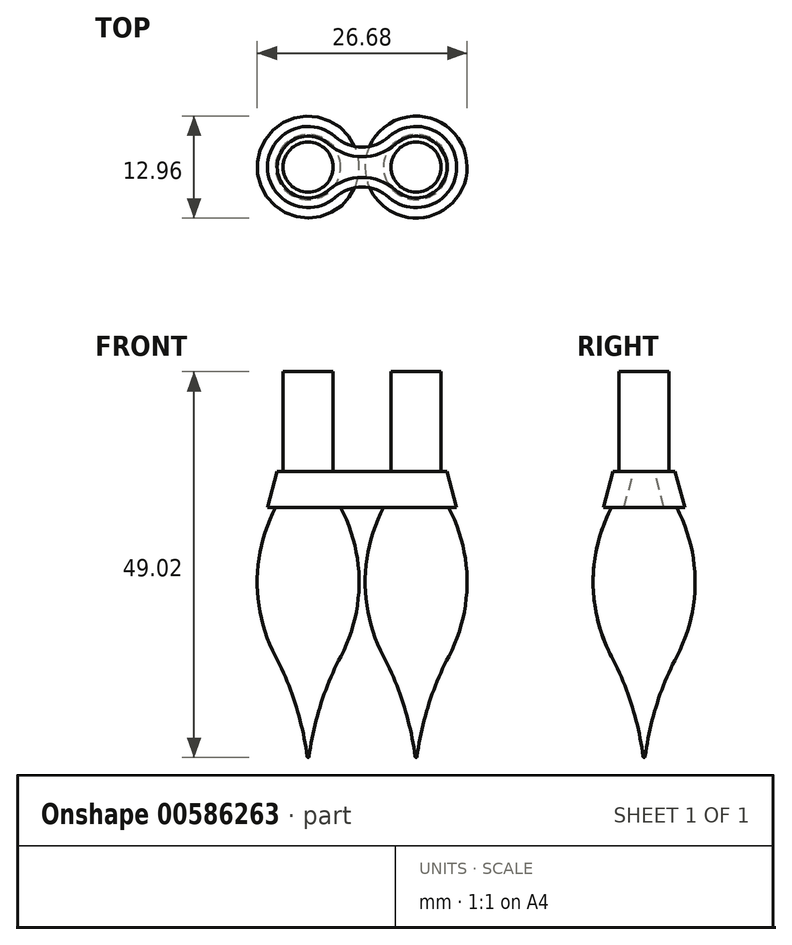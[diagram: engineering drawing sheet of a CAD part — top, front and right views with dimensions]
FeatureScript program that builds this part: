
annotation { "Feature Type Name" : "Feature", "Feature Type Description" : "" }
export const myFeature = defineFeature(function(context is Context, id is Id, definition is map)
    precondition{}
    {
        {
            var Q0;
            Q0=qCreatedBy(makeId("Front.planeOp"),FACE);
            var sketch = newSketch(context, id + "F0", { "sketchPlane" : qUnion([Q0])});
            skLineSegment(sketch, "E0", {"start": v(-6.86, 23.65) * mm, "end": v(-6.86, -36.32) * mm, "construction": true});
            skLineSegment(sketch, "E1", {"start": v(-10.03, 12.7) * mm, "end": v(-10.03, -4.57) * mm});
            skArc(sketch, "E2", {"start": v(-11, -4.57) * mm, "mid": v(-12.74, -9.16) * mm, "end": v(-13.34, -14.03) * mm});
            skLineSegment(sketch, "E3", {"start": v(-10.03, 12.7) * mm, "end": v(-6.86, 12.7) * mm});
            skLineSegment(sketch, "E4", {"start": v(-6.86, 12.7) * mm, "end": v(-6.86, -36.32) * mm});
            skArc(sketch, "E5", {"start": v(-13.34, -14.03) * mm, "mid": v(-12.75, -18.89) * mm, "end": v(-11.01, -23.46) * mm});
            skLineSegment(sketch, "E6", {"start": v(-13.34, -6.84) * mm, "end": v(-13.33, -21.22) * mm, "construction": true});
            skArc(sketch, "E7", {"start": v(-6.86, -36.32) * mm, "mid": v(-6.94, -36.3) * mm, "end": v(-6.98, -36.21) * mm});
            skArc(sketch, "E8", {"start": v(-6.98, -36.21) * mm, "mid": v(-8.44, -29.66) * mm, "end": v(-11.01, -23.46) * mm});
            skLineSegment(sketch, "E9", {"start": v(-6.86, -36.32) * mm, "end": v(-15.63, -36.32) * mm, "construction": true});
            skPoint(sketch, "E10", {"position": v(-13.34, -14.03) * mm});
            skLineSegment(sketch, "E11", {"start": v(-11, -4.57) * mm, "end": v(-10.03, -4.57) * mm});
            skPoint(sketch, "E12.orphan", {"position": v(-10.03, 0) * mm});
            skSolve(sketch);
        }
        {
            var Q0;
            Q0 = qSketchRegion(id + "F0", true);
            var Q1;
            Q1=sQuery(id+"F0.wireOp",EDGE,"E0");
            revolve(context, id + "F1", {"entities" : qUnion([Q0]), "axis" : qUnion([Q1]), "revolveType" : RevolveType.FULL});
        }
        {
            var Q0;
            Q0=makeQuery(id+"F1.opRevolve","SWEPT_BODY",BODY,{"disambiguationData":[OSD([sQuery(id+"F0.wireOp",EDGE,"E1"),sQuery(id+"F0.wireOp",EDGE,"H9bve8Rt-wg82-Txew-taS0-dXrAGqOwYvel"),sQuery(id+"F0.wireOp",EDGE,"E2"),sQuery(id+"F0.wireOp",EDGE,"E3"),sQuery(id+"F0.wireOp",EDGE,"E4"),sQuery(id+"F0.wireOp",EDGE,"E5"),sQuery(id+"F0.wireOp",EDGE,"E7"),sQuery(id+"F0.wireOp",EDGE,"E8")])]});
            var Q1;
            Q1=qCreatedBy(makeId("Right.planeOp"),FACE);
            mirror(context, id + "F2", {"entities" : qUnion([Q0]), "mirrorPlane" : qUnion([Q1])});
        }
        {
            var Q0;
            Q0=makeQuery(id+"F1.opRevolve","SWEPT_FACE",FACE,{"disambiguationData":[OSD([sQuery(id+"F0.wireOp",EDGE,"E11")])]});
            var sketch = newSketch(context, id + "F3", { "sketchPlane" : qUnion([Q0])});
            skArc(sketch, "E13.0", {"start": v(-3.43, 3.85) * mm, "mid": v(-12.01, 0) * mm, "end": v(-3.43, -3.85) * mm});
            skArc(sketch, "E14.0", {"start": v(3.43, 3.85) * mm, "mid": v(12.01, 0) * mm, "end": v(3.43, -3.85) * mm});
            skArc(sketch, "E15", {"start": v(-3.43, 3.85) * mm, "mid": v(0, 2.55) * mm, "end": v(3.43, 3.85) * mm});
            skLineSegment(sketch, "E16", {"start": v(-6.86, 0) * mm, "end": v(6.86, 0) * mm, "construction": true});
            skArc(sketch, "E17.MirrorCS", {"start": v(-3.43, -3.85) * mm, "mid": v(0, -2.55) * mm, "end": v(3.43, -3.85) * mm});
            skSolve(sketch);
        }
        {
            var Q0;
            Q0 = qSketchRegion(id + "F3", true);
            extrude(context, id + "F4", {"entities" : qUnion([Q0]), "operationType" : NewBodyOperationType.ADD, "depth" : 4.57 * mm, "offsetDistance" : 25.4 * mm, "hasDraft" : true, "draftAngle" : 15 * degree, "draftPullDirection" : true});
        }
    });
